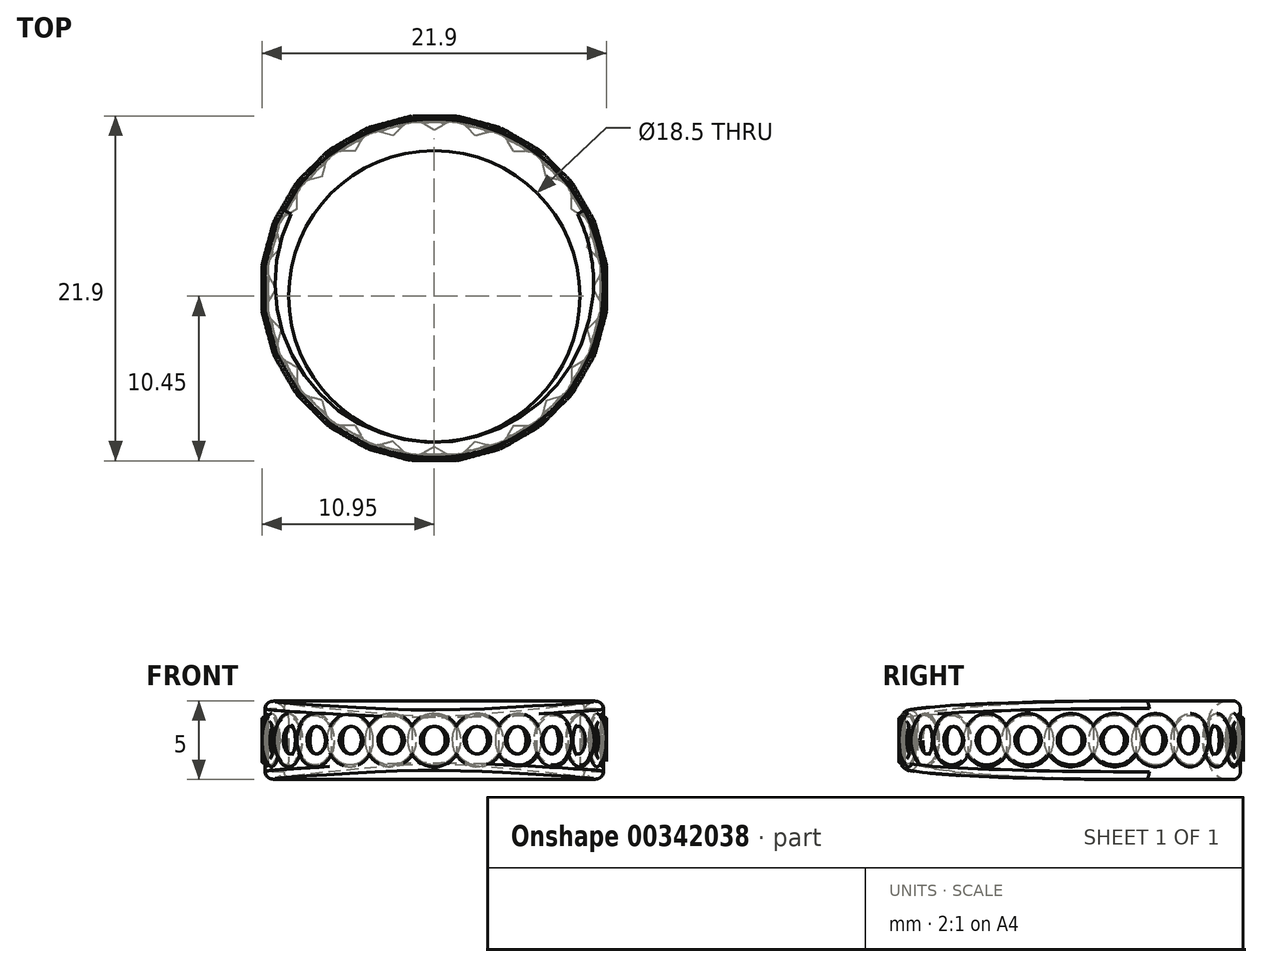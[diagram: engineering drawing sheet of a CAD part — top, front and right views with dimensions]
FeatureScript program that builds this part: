
annotation { "Feature Type Name" : "Feature", "Feature Type Description" : "" }
export const myFeature = defineFeature(function(context is Context, id is Id, definition is map)
    precondition{}
    {
        {
            var Q0;
            Q0=qCreatedBy(makeId("Top.planeOp"),FACE);
            var sketch = newSketch(context, id + "F0", { "sketchPlane" : qUnion([Q0])});
            skCircle(sketch, "E0", {"center": v(0, 0) * mm, "radius": 9.25 * mm});
            skCircle(sketch, "E1.0", {"center": v(0, 0.5) * mm, "radius": 10.75 * mm});
            skSolve(sketch);
        }
        {
            var Q0;
            Q0=makeQuery(id+"F0.imprint","IMPRINT",FACE,{"disambiguationData":[TD([[makeQuery(id+"F0.imprint","IMPRINT",EDGE,{"derivedFrom":sQuery(id+"F0.wireOp",EDGE,"E0")}),-1.0]])]});
            extrude(context, id + "F1", {"entities" : qUnion([Q0]), "endBound" : BoundingType.SYMMETRIC, "depth" : 5 * mm});
        }
        {
            var Q0;
            Q0=makeQuery(id+"F1.opExtrude","CAP_EDGE",EDGE,{"disambiguationData":[OSD([sQuery(id+"F0.wireOp",EDGE,"E0")])],"isStart":false});
            var Q1;
            Q1=makeQuery(id+"F1.opExtrude","CAP_EDGE",EDGE,{"disambiguationData":[OSD([sQuery(id+"F0.wireOp",EDGE,"E0")])],"isStart":true});
            fillet(context, id + "F2", {"entities" : qUnion([Q0, Q1]), "radius" : 1.25 * mm, "tangentPropagation" : true, "allowEdgeOverflow" : false});
        }
        {
            var Q0;
            Q0=makeQuery(id+"F1.opExtrude","CAP_EDGE",EDGE,{"disambiguationData":[OSD([sQuery(id+"F0.wireOp",EDGE,"E1.0")])],"isStart":false});
            var Q1;
            Q1=makeQuery(id+"F1.opExtrude","CAP_EDGE",EDGE,{"disambiguationData":[OSD([sQuery(id+"F0.wireOp",EDGE,"E1.0")])],"isStart":true});
            fillet(context, id + "F3", {"entities" : qUnion([Q0, Q1]), "radius" : 0.49 * mm, "tangentPropagation" : true, "allowEdgeOverflow" : false});
        }
        {
            var Q0;
            Q0=qCreatedBy(makeId("Right.planeOp"),FACE);
            var sketch = newSketch(context, id + "F4", { "sketchPlane" : qUnion([Q0])});
            skLineSegment(sketch, "E2", {"start": v(-10.25, -1.42) * mm, "end": v(-10.25, 1.42) * mm});
            skLineSegment(sketch, "E3", {"start": v(11.25, 2.01) * mm, "end": v(11.25, -2.01) * mm});
            skArc(sketch, "E4", {"start": v(-9.28, 1.53) * mm, "mid": v(-9.82, 1.9) * mm, "end": v(-10.25, 1.42) * mm});
            skArc(sketch, "E5", {"start": v(-10.25, -1.42) * mm, "mid": v(-9.82, -1.9) * mm, "end": v(-9.28, -1.53) * mm});
            skArc(sketch, "E6", {"start": v(10.76, -2.5) * mm, "mid": v(11.1, -2.36) * mm, "end": v(11.25, -2.01) * mm});
            skArc(sketch, "E7", {"start": v(11.25, 2.01) * mm, "mid": v(11.1, 2.36) * mm, "end": v(10.76, 2.5) * mm});
            skPoint(sketch, "E8.0", {"position": v(0.5, 0) * mm});
            skLineSegment(sketch, "E9", {"start": v(0.5, 7.93) * mm, "end": v(0.5, -7.2) * mm, "construction": true});
            skSolve(sketch);
        }
        {
            var Q0;
            Q0=sQuery(id+"F4.wireOp",EDGE,"E3");
            cPlane(context, id + "F5", {"entities" : qUnion([Q0]), "cplaneType" : CPlaneType.LINE_ANGLE, "offset" : 25 * mm, "angle" : 90 * degree, "width" : 150 * mm, "height" : 150 * mm});
        }
        {
            var Q0;
            Q0=qCreatedBy(id+"F5.planeOp",FACE);
            var sketch = newSketch(context, id + "F6", { "sketchPlane" : qUnion([Q0])});
            skCircle(sketch, "E10", {"center": v(0, 0) * mm, "radius": 1.2 * mm});
            skSolve(sketch);
        }
        {
            var Q0;
            Q0=makeQuery(id+"F6.imprint","IMPRINT",FACE,{"disambiguationData":[TD([[makeQuery(id+"F6.imprint","IMPRINT",EDGE,{"derivedFrom":sQuery(id+"F6.wireOp",EDGE,"E10")}),1.0]])]});
            var Q1;
            Q1=makeQuery(id+"F1.opExtrude","SWEPT_FACE",FACE,{"disambiguationData":[OSD([sQuery(id+"F0.wireOp",EDGE,"E0")])]});
            extrude(context, id + "F7", {"entities" : qUnion([Q0]), "oppositeDirection" : true, "endBoundEntityFace" : qUnion([Q1]), "depth" : 0.7 * mm, "hasDraft" : true, "draftAngle" : 60 * degree, "draftPullDirection" : true});
        }
        {
            var Q0;
            Q0=makeQuery(id+"F7.opExtrude","SWEPT_BODY",BODY,{"disambiguationData":[OSD([sQuery(id+"F6.wireOp",EDGE,"E10")])]});
            var Q1;
            Q1=sQuery(id+"F4.wireOp",EDGE,"E9");
            circularPattern(context, id + "F8", {"entities" : qUnion([Q0]), "axis" : qUnion([Q1]), "angle" : 360 * degree, "instanceCount" : 24, "equalSpace" : true});
        }
        {
            var Q0;
            Q0=makeQuery(id+"F7.opExtrude","SWEPT_BODY",BODY,{"disambiguationData":[OSD([sQuery(id+"F6.wireOp",EDGE,"E10")])]});
            var Q1;
            Q1=makeQuery(id+"F8.opPattern","COPY",BODY,{"derivedFrom":makeQuery(id+"F7.opExtrude","SWEPT_BODY",BODY,{"disambiguationData":[OSD([sQuery(id+"F6.wireOp",EDGE,"E10")])]}),"instanceName":"1"});
            var Q2;
            Q2=makeQuery(id+"F8.opPattern","COPY",BODY,{"derivedFrom":makeQuery(id+"F7.opExtrude","SWEPT_BODY",BODY,{"disambiguationData":[OSD([sQuery(id+"F6.wireOp",EDGE,"E10")])]}),"instanceName":"2"});
            var Q3;
            Q3=makeQuery(id+"F8.opPattern","COPY",BODY,{"derivedFrom":makeQuery(id+"F7.opExtrude","SWEPT_BODY",BODY,{"disambiguationData":[OSD([sQuery(id+"F6.wireOp",EDGE,"E10")])]}),"instanceName":"3"});
            var Q4;
            Q4=makeQuery(id+"F8.opPattern","COPY",BODY,{"derivedFrom":makeQuery(id+"F7.opExtrude","SWEPT_BODY",BODY,{"disambiguationData":[OSD([sQuery(id+"F6.wireOp",EDGE,"E10")])]}),"instanceName":"4"});
            var Q5;
            Q5=makeQuery(id+"F8.opPattern","COPY",BODY,{"derivedFrom":makeQuery(id+"F7.opExtrude","SWEPT_BODY",BODY,{"disambiguationData":[OSD([sQuery(id+"F6.wireOp",EDGE,"E10")])]}),"instanceName":"5"});
            var Q6;
            Q6=makeQuery(id+"F8.opPattern","COPY",BODY,{"derivedFrom":makeQuery(id+"F7.opExtrude","SWEPT_BODY",BODY,{"disambiguationData":[OSD([sQuery(id+"F6.wireOp",EDGE,"E10")])]}),"instanceName":"6"});
            var Q7;
            Q7=makeQuery(id+"F8.opPattern","COPY",BODY,{"derivedFrom":makeQuery(id+"F7.opExtrude","SWEPT_BODY",BODY,{"disambiguationData":[OSD([sQuery(id+"F6.wireOp",EDGE,"E10")])]}),"instanceName":"7"});
            var Q8;
            Q8=makeQuery(id+"F8.opPattern","COPY",BODY,{"derivedFrom":makeQuery(id+"F7.opExtrude","SWEPT_BODY",BODY,{"disambiguationData":[OSD([sQuery(id+"F6.wireOp",EDGE,"E10")])]}),"instanceName":"8"});
            var Q9;
            Q9=makeQuery(id+"F8.opPattern","COPY",BODY,{"derivedFrom":makeQuery(id+"F7.opExtrude","SWEPT_BODY",BODY,{"disambiguationData":[OSD([sQuery(id+"F6.wireOp",EDGE,"E10")])]}),"instanceName":"9"});
            var Q10;
            Q10=makeQuery(id+"F8.opPattern","COPY",BODY,{"derivedFrom":makeQuery(id+"F7.opExtrude","SWEPT_BODY",BODY,{"disambiguationData":[OSD([sQuery(id+"F6.wireOp",EDGE,"E10")])]}),"instanceName":"10"});
            var Q11;
            Q11=makeQuery(id+"F8.opPattern","COPY",BODY,{"derivedFrom":makeQuery(id+"F7.opExtrude","SWEPT_BODY",BODY,{"disambiguationData":[OSD([sQuery(id+"F6.wireOp",EDGE,"E10")])]}),"instanceName":"11"});
            var Q12;
            Q12=makeQuery(id+"F8.opPattern","COPY",BODY,{"derivedFrom":makeQuery(id+"F7.opExtrude","SWEPT_BODY",BODY,{"disambiguationData":[OSD([sQuery(id+"F6.wireOp",EDGE,"E10")])]}),"instanceName":"12"});
            var Q13;
            Q13=makeQuery(id+"F8.opPattern","COPY",BODY,{"derivedFrom":makeQuery(id+"F7.opExtrude","SWEPT_BODY",BODY,{"disambiguationData":[OSD([sQuery(id+"F6.wireOp",EDGE,"E10")])]}),"instanceName":"13"});
            var Q14;
            Q14=makeQuery(id+"F8.opPattern","COPY",BODY,{"derivedFrom":makeQuery(id+"F7.opExtrude","SWEPT_BODY",BODY,{"disambiguationData":[OSD([sQuery(id+"F6.wireOp",EDGE,"E10")])]}),"instanceName":"14"});
            var Q15;
            Q15=makeQuery(id+"F8.opPattern","COPY",BODY,{"derivedFrom":makeQuery(id+"F7.opExtrude","SWEPT_BODY",BODY,{"disambiguationData":[OSD([sQuery(id+"F6.wireOp",EDGE,"E10")])]}),"instanceName":"15"});
            var Q16;
            Q16=makeQuery(id+"F8.opPattern","COPY",BODY,{"derivedFrom":makeQuery(id+"F7.opExtrude","SWEPT_BODY",BODY,{"disambiguationData":[OSD([sQuery(id+"F6.wireOp",EDGE,"E10")])]}),"instanceName":"16"});
            var Q17;
            Q17=makeQuery(id+"F8.opPattern","COPY",BODY,{"derivedFrom":makeQuery(id+"F7.opExtrude","SWEPT_BODY",BODY,{"disambiguationData":[OSD([sQuery(id+"F6.wireOp",EDGE,"E10")])]}),"instanceName":"17"});
            var Q18;
            Q18=makeQuery(id+"F8.opPattern","COPY",BODY,{"derivedFrom":makeQuery(id+"F7.opExtrude","SWEPT_BODY",BODY,{"disambiguationData":[OSD([sQuery(id+"F6.wireOp",EDGE,"E10")])]}),"instanceName":"18"});
            var Q19;
            Q19=makeQuery(id+"F8.opPattern","COPY",BODY,{"derivedFrom":makeQuery(id+"F7.opExtrude","SWEPT_BODY",BODY,{"disambiguationData":[OSD([sQuery(id+"F6.wireOp",EDGE,"E10")])]}),"instanceName":"19"});
            var Q20;
            Q20=makeQuery(id+"F8.opPattern","COPY",BODY,{"derivedFrom":makeQuery(id+"F7.opExtrude","SWEPT_BODY",BODY,{"disambiguationData":[OSD([sQuery(id+"F6.wireOp",EDGE,"E10")])]}),"instanceName":"20"});
            var Q21;
            Q21=makeQuery(id+"F8.opPattern","COPY",BODY,{"derivedFrom":makeQuery(id+"F7.opExtrude","SWEPT_BODY",BODY,{"disambiguationData":[OSD([sQuery(id+"F6.wireOp",EDGE,"E10")])]}),"instanceName":"21"});
            var Q22;
            Q22=makeQuery(id+"F8.opPattern","COPY",BODY,{"derivedFrom":makeQuery(id+"F7.opExtrude","SWEPT_BODY",BODY,{"disambiguationData":[OSD([sQuery(id+"F6.wireOp",EDGE,"E10")])]}),"instanceName":"22"});
            var Q23;
            Q23=makeQuery(id+"F8.opPattern","COPY",BODY,{"derivedFrom":makeQuery(id+"F7.opExtrude","SWEPT_BODY",BODY,{"disambiguationData":[OSD([sQuery(id+"F6.wireOp",EDGE,"E10")])]}),"instanceName":"23"});
            var Q24;
            Q24=makeQuery(id+"F1.opExtrude","SWEPT_BODY",BODY,{"disambiguationData":[OSD([sQuery(id+"F0.wireOp",EDGE,"E0"),sQuery(id+"F0.wireOp",EDGE,"E1.0")])]});
            booleanBodies(context, id + "F9", {"operationType" : BooleanOperationType.SUBTRACTION, "tools" : qUnion([Q0, Q1, Q2, Q3, Q4, Q5, Q6, Q7, Q8, Q9, Q10, Q11, Q12, Q13, Q14, Q15, Q16, Q17, Q18, Q19, Q20, Q21, Q22, Q23]), "targets" : qUnion([Q24])});
        }
        {
            var Q0;
            Q0=makeQuery(id+"F9.opBoolean","INTERSECT",EDGE,{"derivedFrom":[makeQuery(id+"F1.opExtrude","SWEPT_FACE",FACE,{"disambiguationData":[OSD([sQuery(id+"F0.wireOp",EDGE,"E1.0")])]}),makeQuery(id+"F8.opPattern","COPY",FACE,{"derivedFrom":makeQuery(id+"F7.opExtrude","SWEPT_FACE",FACE,{"disambiguationData":[OSD([sQuery(id+"F6.wireOp",EDGE,"E10")])]}),"instanceName":"1"})]});
            var Q1;
            Q1=makeQuery(id+"F9.opBoolean","INTERSECT",EDGE,{"derivedFrom":[makeQuery(id+"F1.opExtrude","SWEPT_FACE",FACE,{"disambiguationData":[OSD([sQuery(id+"F0.wireOp",EDGE,"E1.0")])]}),makeQuery(id+"F8.opPattern","COPY",FACE,{"derivedFrom":makeQuery(id+"F7.opExtrude","SWEPT_FACE",FACE,{"disambiguationData":[OSD([sQuery(id+"F6.wireOp",EDGE,"E10")])]}),"instanceName":"2"})]});
            var Q2;
            Q2=makeQuery(id+"F9.opBoolean","INTERSECT",EDGE,{"derivedFrom":[makeQuery(id+"F1.opExtrude","SWEPT_FACE",FACE,{"disambiguationData":[OSD([sQuery(id+"F0.wireOp",EDGE,"E1.0")])]}),makeQuery(id+"F7.opExtrude","SWEPT_FACE",FACE,{"disambiguationData":[OSD([sQuery(id+"F6.wireOp",EDGE,"E10")])]})]});
            var Q3;
            Q3=makeQuery(id+"F9.opBoolean","INTERSECT",EDGE,{"derivedFrom":[makeQuery(id+"F1.opExtrude","SWEPT_FACE",FACE,{"disambiguationData":[OSD([sQuery(id+"F0.wireOp",EDGE,"E1.0")])]}),makeQuery(id+"F8.opPattern","COPY",FACE,{"derivedFrom":makeQuery(id+"F7.opExtrude","SWEPT_FACE",FACE,{"disambiguationData":[OSD([sQuery(id+"F6.wireOp",EDGE,"E10")])]}),"instanceName":"23"})]});
            var Q4;
            Q4=makeQuery(id+"F9.opBoolean","INTERSECT",EDGE,{"derivedFrom":[makeQuery(id+"F1.opExtrude","SWEPT_FACE",FACE,{"disambiguationData":[OSD([sQuery(id+"F0.wireOp",EDGE,"E1.0")])]}),makeQuery(id+"F8.opPattern","COPY",FACE,{"derivedFrom":makeQuery(id+"F7.opExtrude","SWEPT_FACE",FACE,{"disambiguationData":[OSD([sQuery(id+"F6.wireOp",EDGE,"E10")])]}),"instanceName":"3"})]});
            var Q5;
            Q5=makeQuery(id+"F9.opBoolean","INTERSECT",EDGE,{"derivedFrom":[makeQuery(id+"F1.opExtrude","SWEPT_FACE",FACE,{"disambiguationData":[OSD([sQuery(id+"F0.wireOp",EDGE,"E1.0")])]}),makeQuery(id+"F8.opPattern","COPY",FACE,{"derivedFrom":makeQuery(id+"F7.opExtrude","SWEPT_FACE",FACE,{"disambiguationData":[OSD([sQuery(id+"F6.wireOp",EDGE,"E10")])]}),"instanceName":"4"})]});
            var Q6;
            Q6=makeQuery(id+"F9.opBoolean","INTERSECT",EDGE,{"derivedFrom":[makeQuery(id+"F1.opExtrude","SWEPT_FACE",FACE,{"disambiguationData":[OSD([sQuery(id+"F0.wireOp",EDGE,"E1.0")])]}),makeQuery(id+"F8.opPattern","COPY",FACE,{"derivedFrom":makeQuery(id+"F7.opExtrude","SWEPT_FACE",FACE,{"disambiguationData":[OSD([sQuery(id+"F6.wireOp",EDGE,"E10")])]}),"instanceName":"5"})]});
            var Q7;
            Q7=makeQuery(id+"F9.opBoolean","INTERSECT",EDGE,{"derivedFrom":[makeQuery(id+"F1.opExtrude","SWEPT_FACE",FACE,{"disambiguationData":[OSD([sQuery(id+"F0.wireOp",EDGE,"E1.0")])]}),makeQuery(id+"F8.opPattern","COPY",FACE,{"derivedFrom":makeQuery(id+"F7.opExtrude","SWEPT_FACE",FACE,{"disambiguationData":[OSD([sQuery(id+"F6.wireOp",EDGE,"E10")])]}),"instanceName":"6"})]});
            var Q8;
            Q8=makeQuery(id+"F9.opBoolean","INTERSECT",EDGE,{"derivedFrom":[makeQuery(id+"F1.opExtrude","SWEPT_FACE",FACE,{"disambiguationData":[OSD([sQuery(id+"F0.wireOp",EDGE,"E1.0")])]}),makeQuery(id+"F8.opPattern","COPY",FACE,{"derivedFrom":makeQuery(id+"F7.opExtrude","SWEPT_FACE",FACE,{"disambiguationData":[OSD([sQuery(id+"F6.wireOp",EDGE,"E10")])]}),"instanceName":"7"})]});
            var Q9;
            Q9=makeQuery(id+"F9.opBoolean","INTERSECT",EDGE,{"derivedFrom":[makeQuery(id+"F1.opExtrude","SWEPT_FACE",FACE,{"disambiguationData":[OSD([sQuery(id+"F0.wireOp",EDGE,"E1.0")])]}),makeQuery(id+"F8.opPattern","COPY",FACE,{"derivedFrom":makeQuery(id+"F7.opExtrude","SWEPT_FACE",FACE,{"disambiguationData":[OSD([sQuery(id+"F6.wireOp",EDGE,"E10")])]}),"instanceName":"22"})]});
            var Q10;
            Q10=makeQuery(id+"F9.opBoolean","INTERSECT",EDGE,{"derivedFrom":[makeQuery(id+"F1.opExtrude","SWEPT_FACE",FACE,{"disambiguationData":[OSD([sQuery(id+"F0.wireOp",EDGE,"E1.0")])]}),makeQuery(id+"F8.opPattern","COPY",FACE,{"derivedFrom":makeQuery(id+"F7.opExtrude","SWEPT_FACE",FACE,{"disambiguationData":[OSD([sQuery(id+"F6.wireOp",EDGE,"E10")])]}),"instanceName":"21"})]});
            var Q11;
            Q11=makeQuery(id+"F9.opBoolean","INTERSECT",EDGE,{"derivedFrom":[makeQuery(id+"F1.opExtrude","SWEPT_FACE",FACE,{"disambiguationData":[OSD([sQuery(id+"F0.wireOp",EDGE,"E1.0")])]}),makeQuery(id+"F8.opPattern","COPY",FACE,{"derivedFrom":makeQuery(id+"F7.opExtrude","SWEPT_FACE",FACE,{"disambiguationData":[OSD([sQuery(id+"F6.wireOp",EDGE,"E10")])]}),"instanceName":"20"})]});
            var Q12;
            Q12=makeQuery(id+"F9.opBoolean","INTERSECT",EDGE,{"derivedFrom":[makeQuery(id+"F1.opExtrude","SWEPT_FACE",FACE,{"disambiguationData":[OSD([sQuery(id+"F0.wireOp",EDGE,"E1.0")])]}),makeQuery(id+"F8.opPattern","COPY",FACE,{"derivedFrom":makeQuery(id+"F7.opExtrude","SWEPT_FACE",FACE,{"disambiguationData":[OSD([sQuery(id+"F6.wireOp",EDGE,"E10")])]}),"instanceName":"19"})]});
            var Q13;
            Q13=makeQuery(id+"F9.opBoolean","INTERSECT",EDGE,{"derivedFrom":[makeQuery(id+"F1.opExtrude","SWEPT_FACE",FACE,{"disambiguationData":[OSD([sQuery(id+"F0.wireOp",EDGE,"E1.0")])]}),makeQuery(id+"F8.opPattern","COPY",FACE,{"derivedFrom":makeQuery(id+"F7.opExtrude","SWEPT_FACE",FACE,{"disambiguationData":[OSD([sQuery(id+"F6.wireOp",EDGE,"E10")])]}),"instanceName":"18"})]});
            var Q14;
            Q14=makeQuery(id+"F9.opBoolean","INTERSECT",EDGE,{"derivedFrom":[makeQuery(id+"F1.opExtrude","SWEPT_FACE",FACE,{"disambiguationData":[OSD([sQuery(id+"F0.wireOp",EDGE,"E1.0")])]}),makeQuery(id+"F8.opPattern","COPY",FACE,{"derivedFrom":makeQuery(id+"F7.opExtrude","SWEPT_FACE",FACE,{"disambiguationData":[OSD([sQuery(id+"F6.wireOp",EDGE,"E10")])]}),"instanceName":"17"})]});
            var Q15;
            Q15=makeQuery(id+"F9.opBoolean","INTERSECT",EDGE,{"derivedFrom":[makeQuery(id+"F1.opExtrude","SWEPT_FACE",FACE,{"disambiguationData":[OSD([sQuery(id+"F0.wireOp",EDGE,"E1.0")])]}),makeQuery(id+"F8.opPattern","COPY",FACE,{"derivedFrom":makeQuery(id+"F7.opExtrude","SWEPT_FACE",FACE,{"disambiguationData":[OSD([sQuery(id+"F6.wireOp",EDGE,"E10")])]}),"instanceName":"16"})]});
            var Q16;
            Q16=makeQuery(id+"F9.opBoolean","INTERSECT",EDGE,{"derivedFrom":[makeQuery(id+"F1.opExtrude","SWEPT_FACE",FACE,{"disambiguationData":[OSD([sQuery(id+"F0.wireOp",EDGE,"E1.0")])]}),makeQuery(id+"F8.opPattern","COPY",FACE,{"derivedFrom":makeQuery(id+"F7.opExtrude","SWEPT_FACE",FACE,{"disambiguationData":[OSD([sQuery(id+"F6.wireOp",EDGE,"E10")])]}),"instanceName":"15"})]});
            var Q17;
            Q17=makeQuery(id+"F9.opBoolean","INTERSECT",EDGE,{"derivedFrom":[makeQuery(id+"F1.opExtrude","SWEPT_FACE",FACE,{"disambiguationData":[OSD([sQuery(id+"F0.wireOp",EDGE,"E1.0")])]}),makeQuery(id+"F8.opPattern","COPY",FACE,{"derivedFrom":makeQuery(id+"F7.opExtrude","SWEPT_FACE",FACE,{"disambiguationData":[OSD([sQuery(id+"F6.wireOp",EDGE,"E10")])]}),"instanceName":"14"})]});
            var Q18;
            Q18=makeQuery(id+"F9.opBoolean","INTERSECT",EDGE,{"derivedFrom":[makeQuery(id+"F1.opExtrude","SWEPT_FACE",FACE,{"disambiguationData":[OSD([sQuery(id+"F0.wireOp",EDGE,"E1.0")])]}),makeQuery(id+"F8.opPattern","COPY",FACE,{"derivedFrom":makeQuery(id+"F7.opExtrude","SWEPT_FACE",FACE,{"disambiguationData":[OSD([sQuery(id+"F6.wireOp",EDGE,"E10")])]}),"instanceName":"13"})]});
            var Q19;
            Q19=makeQuery(id+"F9.opBoolean","INTERSECT",EDGE,{"derivedFrom":[makeQuery(id+"F1.opExtrude","SWEPT_FACE",FACE,{"disambiguationData":[OSD([sQuery(id+"F0.wireOp",EDGE,"E1.0")])]}),makeQuery(id+"F8.opPattern","COPY",FACE,{"derivedFrom":makeQuery(id+"F7.opExtrude","SWEPT_FACE",FACE,{"disambiguationData":[OSD([sQuery(id+"F6.wireOp",EDGE,"E10")])]}),"instanceName":"12"})]});
            var Q20;
            Q20=makeQuery(id+"F9.opBoolean","INTERSECT",EDGE,{"derivedFrom":[makeQuery(id+"F1.opExtrude","SWEPT_FACE",FACE,{"disambiguationData":[OSD([sQuery(id+"F0.wireOp",EDGE,"E1.0")])]}),makeQuery(id+"F8.opPattern","COPY",FACE,{"derivedFrom":makeQuery(id+"F7.opExtrude","SWEPT_FACE",FACE,{"disambiguationData":[OSD([sQuery(id+"F6.wireOp",EDGE,"E10")])]}),"instanceName":"11"})]});
            var Q21;
            Q21=makeQuery(id+"F9.opBoolean","INTERSECT",EDGE,{"derivedFrom":[makeQuery(id+"F1.opExtrude","SWEPT_FACE",FACE,{"disambiguationData":[OSD([sQuery(id+"F0.wireOp",EDGE,"E1.0")])]}),makeQuery(id+"F8.opPattern","COPY",FACE,{"derivedFrom":makeQuery(id+"F7.opExtrude","SWEPT_FACE",FACE,{"disambiguationData":[OSD([sQuery(id+"F6.wireOp",EDGE,"E10")])]}),"instanceName":"10"})]});
            var Q22;
            Q22=makeQuery(id+"F9.opBoolean","INTERSECT",EDGE,{"derivedFrom":[makeQuery(id+"F1.opExtrude","SWEPT_FACE",FACE,{"disambiguationData":[OSD([sQuery(id+"F0.wireOp",EDGE,"E1.0")])]}),makeQuery(id+"F8.opPattern","COPY",FACE,{"derivedFrom":makeQuery(id+"F7.opExtrude","SWEPT_FACE",FACE,{"disambiguationData":[OSD([sQuery(id+"F6.wireOp",EDGE,"E10")])]}),"instanceName":"9"})]});
            var Q23;
            Q23=makeQuery(id+"F9.opBoolean","INTERSECT",EDGE,{"derivedFrom":[makeQuery(id+"F1.opExtrude","SWEPT_FACE",FACE,{"disambiguationData":[OSD([sQuery(id+"F0.wireOp",EDGE,"E1.0")])]}),makeQuery(id+"F8.opPattern","COPY",FACE,{"derivedFrom":makeQuery(id+"F7.opExtrude","SWEPT_FACE",FACE,{"disambiguationData":[OSD([sQuery(id+"F6.wireOp",EDGE,"E10")])]}),"instanceName":"8"})]});
            fillet(context, id + "F10", {"entities" : qUnion([Q0, Q1, Q2, Q3, Q4, Q5, Q6, Q7, Q8, Q9, Q10, Q11, Q12, Q13, Q14, Q15, Q16, Q17, Q18, Q19, Q20, Q21, Q22, Q23]), "radius" : 1.4 * mm, "tangentPropagation" : true, "allowEdgeOverflow" : false});
        }
        {
            var Q0;
            Q0=qCreatedBy(id+"F5.planeOp",FACE);
            var sketch = newSketch(context, id + "F11", { "sketchPlane" : qUnion([Q0])});
            skCircle(sketch, "E11.0", {"center": v(0, 0) * mm, "radius": 1.2 * mm, "construction": true});
            skCircle(sketch, "E12.0", {"center": v(0, 0) * mm, "radius": 1.38 * mm});
            skSolve(sketch);
        }
        {
            var Q0;
            Q0=qCreatedBy(makeId("Right.planeOp"),FACE);
            var sketch = newSketch(context, id + "F12", { "sketchPlane" : qUnion([Q0])});
            skArc(sketch, "E13", {"start": v(11.25, -1.58) * mm, "mid": v(11.2, -1.21) * mm, "end": v(11.06, -0.88) * mm, "construction": true});
            skArc(sketch, "E14", {"start": v(11.06, 0.88) * mm, "mid": v(11.2, 1.21) * mm, "end": v(11.25, 1.58) * mm, "construction": true});
            skLineSegment(sketch, "E15", {"start": v(11.25, 2.01) * mm, "end": v(11.25, 1.58) * mm, "construction": true});
            skLineSegment(sketch, "E16", {"start": v(11.06, 1.38) * mm, "end": v(11.06, 0.88) * mm});
            skFitSpline(sketch, "E17", {"points": [v(11.06, 0.88) * mm, v(11.45, 1.37) * mm, v(11.25, 1.6) * mm], "startDerivative": vector(0.64, 1.11) * mm, "endDerivative": vector(0, 0.9) * mm});
            skFitSpline(sketch, "E18", {"points": [v(11.25, 1.6) * mm, v(11.06, 1.38) * mm], "startDerivative": vector(0, 0.48) * mm, "endDerivative": vector(0, -1) * mm});
            skPoint(sketch, "E19", {"position": v(11.25, 1.8) * mm});
            skSolve(sketch);
        }
        {
            var Q0;
            Q0=qSketchRegion(id+"F12",true);
            var Q1;
            Q1=sQuery(id+"F11.wireOp",EDGE,"E12.0");
            sweep(context, id + "F13", {"profiles" : qUnion([Q0]), "path" : qUnion([Q1])});
        }
        {
            var Q0;
            Q0=makeQuery(id+"F13.opSweep","SWEPT_BODY",BODY,{"disambiguationData":[OSD([sQuery(id+"F11.wireOp",EDGE,"E12.0"),sQuery(id+"F12.wireOp",EDGE,"Dfnfzrhn-J666-IU6h-2tCP-u7NBH7JF8NC0")])]});
            var Q1;
            Q1=sQuery(id+"F4.wireOp",EDGE,"E9");
            circularPattern(context, id + "F14", {"entities" : qUnion([Q0]), "axis" : qUnion([Q1]), "angle" : 360 * degree, "instanceCount" : 24, "equalSpace" : true});
        }
    });
